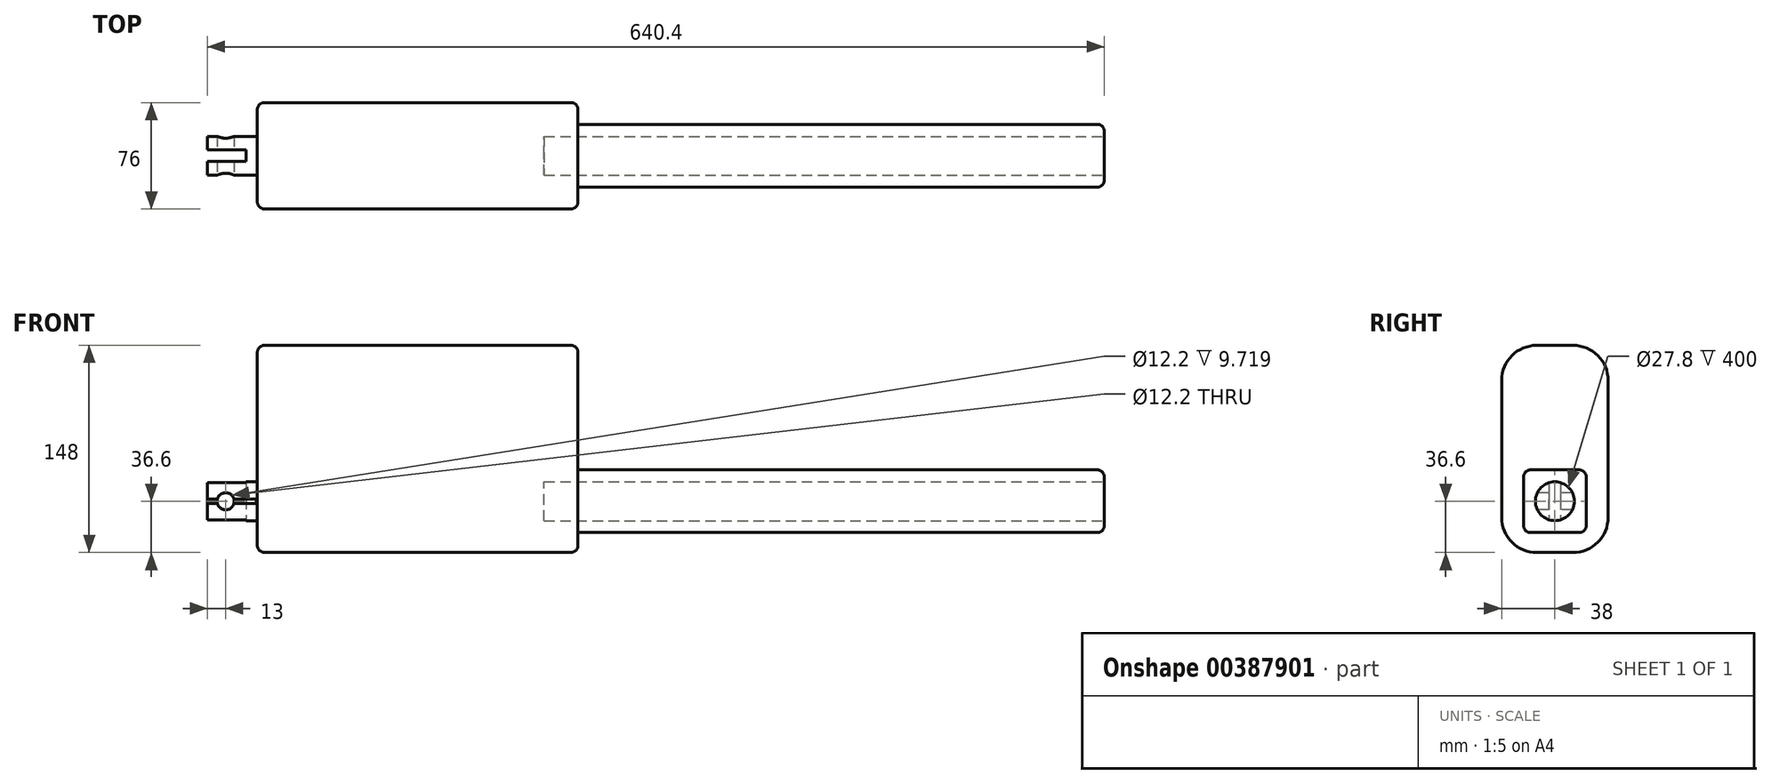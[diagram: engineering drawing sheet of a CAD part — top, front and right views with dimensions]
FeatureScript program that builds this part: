
annotation { "Feature Type Name" : "Feature", "Feature Type Description" : "" }
export const myFeature = defineFeature(function(context is Context, id is Id, definition is map)
    precondition{}
    {
        {
            var Q0;
            Q0=qCreatedBy(makeId("Front.planeOp"),FACE);
            var sketch = newSketch(context, id + "F0", { "sketchPlane" : qUnion([Q0])});
            skLineSegment(sketch, "E0.bottom", {"start": v(-114.5, 74) * mm, "end": v(114.5, 74) * mm});
            skLineSegment(sketch, "E0.top", {"start": v(-114.5, -74) * mm, "end": v(114.5, -74) * mm});
            skLineSegment(sketch, "E0.left", {"start": v(-114.5, 74) * mm, "end": v(-114.5, -74) * mm});
            skLineSegment(sketch, "E0.right", {"start": v(114.5, 74) * mm, "end": v(114.5, -74) * mm});
            skPoint(sketch, "E0.middle", {"position": v(0, 0) * mm});
            skSolve(sketch);
        }
        {
            var Q0;
            Q0=makeQuery(id+"F0.imprint","IMPRINT",FACE,{"disambiguationData":[TD([[makeQuery(id+"F0.imprint","IMPRINT",EDGE,{"derivedFrom":sQuery(id+"F0.wireOp",EDGE,"E0.bottom")}),-1.0]])]});
            extrude(context, id + "F1", {"entities" : qUnion([Q0]), "depth" : 76 * mm, "symmetric" : true});
        }
        {
            var Q0;
            Q0=makeQuery(id+"F1.opExtrude","SWEPT_FACE",FACE,{"disambiguationData":[OSD([sQuery(id+"F0.wireOp",EDGE,"E0.left")])]});
            var sketch = newSketch(context, id + "F2", { "sketchPlane" : qUnion([Q0])});
            skLineSegment(sketch, "E1", {"start": v(0, -74) * mm, "end": v(0, -37.4) * mm});
            skPoint(sketch, "E1.endSnap0", {"position": v(0, -74) * mm});
            skCircle(sketch, "E2", {"center": v(0, -37.4) * mm, "radius": 13.9 * mm});
            skSolve(sketch);
        }
        {
            var Q0;
            Q0=makeQuery(id+"F2.imprint","IMPRINT",FACE,{"disambiguationData":[TD([[makeQuery(id+"F2.imprint","IMPRINT",EDGE,{"derivedFrom":sQuery(id+"F2.wireOp",EDGE,"E2")}),1.0]])]});
            extrude(context, id + "F3", {"entities" : qUnion([Q0]), "operationType" : NewBodyOperationType.ADD, "depth" : 35.6 * mm});
        }
        {
            var Q0;
            Q0=makeQuery(id+"F3.opExtrude","CAP_FACE",FACE,{"disambiguationData":[OSD([sQuery(id+"F2.wireOp",EDGE,"E2")])],"isStart":false});
            var sketch = newSketch(context, id + "F4", { "sketchPlane" : qUnion([Q0])});
            skLineSegment(sketch, "E3.left", {"start": v(-13.82, -35.9) * mm, "end": v(-13.82, -38.9) * mm});
            skLineSegment(sketch, "E3.right", {"start": v(13.82, -35.9) * mm, "end": v(13.82, -38.9) * mm});
            skPoint(sketch, "E3.middle", {"position": v(0, -37.4) * mm});
            skSolve(sketch);
        }
        {
            var Q0;
            {var subQ0=sQuery(id+"F4.wireOp",EDGE,"E3.right");Q0=makeQuery(id+"F4.imprint","IMPRINT",FACE,{"disambiguationData":[TD([[makeQuery(id+"F4.imprint","IMPRINT",EDGE,{"derivedFrom":subQ0}),1.0]])]});}
            extrude(context, id + "F5", {"entities" : qUnion([Q0]), "operationType" : NewBodyOperationType.REMOVE, "oppositeDirection" : true, "depth" : 35 * mm});
        }
        {
            var Q0;
            Q0=makeQuery(id+"F5.boolean.opBoolean","COPY",FACE,{"derivedFrom":makeQuery(id+"F5.opExtrude","SWEPT_FACE",FACE,{"disambiguationData":[OSD([sQuery(id+"F4.wireOp",EDGE,"E3.right")])]})});
            var sketch = newSketch(context, id + "F6", { "sketchPlane" : qUnion([Q0])});
            skLineSegment(sketch, "E4", {"start": v(-150.1, -37.4) * mm, "end": v(-137.1, -37.4) * mm});
            skSolve(sketch);
        }
        {
            var Q0;
            Q0=sQuery(id+"F6.wireOp",VERTEX,"E4.end");
            var Q1;
            Q1=makeQuery(id+"F1.opExtrude","SWEPT_BODY",BODY,{"disambiguationData":[OSD([sQuery(id+"F0.wireOp",EDGE,"E0.bottom"),sQuery(id+"F0.wireOp",EDGE,"E0.top"),sQuery(id+"F0.wireOp",EDGE,"E0.left"),sQuery(id+"F0.wireOp",EDGE,"E0.right")])]});
            hole(context, id + "F7", {"style" : HoleStyle.SIMPLE, "endStyle" : HoleEndStyle.THROUGH, "holeDiameter" : 12.2 * mm, "isTappedThrough" : true, "tappedDepth" : 12 * mm, "tapClearance" : 3, "locations" : qUnion([Q0]), "scope" : qUnion([Q1])});
        }
        {
            var Q0;
            Q0=makeQuery(id+"F1.opExtrude","SWEPT_FACE",FACE,{"disambiguationData":[OSD([sQuery(id+"F0.wireOp",EDGE,"E0.right")])]});
            var sketch = newSketch(context, id + "F8", { "sketchPlane" : qUnion([Q0])});
            skLineSegment(sketch, "E5", {"start": v(0, -74) * mm, "end": v(0, -37.4) * mm});
            skLineSegment(sketch, "E6.bottom", {"start": v(-22.4, -15) * mm, "end": v(22.4, -15) * mm});
            skLineSegment(sketch, "E6.top", {"start": v(-22.4, -59.8) * mm, "end": v(22.4, -59.8) * mm});
            skLineSegment(sketch, "E6.left", {"start": v(-22.4, -15) * mm, "end": v(-22.4, -59.8) * mm});
            skLineSegment(sketch, "E6.right", {"start": v(22.4, -15) * mm, "end": v(22.4, -59.8) * mm});
            skPoint(sketch, "E6.middle", {"position": v(0, -37.4) * mm});
            skSolve(sketch);
        }
        {
            var Q0;
            Q0=makeQuery(id+"F8.imprint","IMPRINT",FACE,{"disambiguationData":[TD([[makeQuery(id+"F8.imprint","IMPRINT",EDGE,{"derivedFrom":sQuery(id+"F8.wireOp",EDGE,"E6.bottom")}),-1.0]])]});
            extrude(context, id + "F9", {"entities" : qUnion([Q0]), "operationType" : NewBodyOperationType.ADD, "depth" : 375.8 * mm});
        }
        {
            var Q0;
            Q0=makeQuery(id+"F9.opExtrude","CAP_FACE",FACE,{"disambiguationData":[OSD([sQuery(id+"F8.wireOp",EDGE,"E6.bottom"),sQuery(id+"F8.wireOp",EDGE,"E6.top"),sQuery(id+"F8.wireOp",EDGE,"E6.left"),sQuery(id+"F8.wireOp",EDGE,"E6.right")])],"isStart":false});
            var sketch = newSketch(context, id + "F10", { "sketchPlane" : qUnion([Q0])});
            skLineSegment(sketch, "E7", {"start": v(0, -15) * mm, "end": v(0, -37.4) * mm});
            skPoint(sketch, "E7.endSnap0", {"position": v(0, -15) * mm});
            skCircle(sketch, "E8", {"center": v(0, -37.4) * mm, "radius": 13.9 * mm});
            skSolve(sketch);
        }
        {
            var Q0;
            Q0=makeQuery(id+"F1.opExtrude","CAP_EDGE",EDGE,{"disambiguationData":[OSD([sQuery(id+"F0.wireOp",EDGE,"E0.bottom")])],"isStart":false});
            var Q1;
            Q1=makeQuery(id+"F1.opExtrude","CAP_EDGE",EDGE,{"disambiguationData":[OSD([sQuery(id+"F0.wireOp",EDGE,"E0.bottom")])],"isStart":true});
            var Q2;
            Q2=makeQuery(id+"F1.opExtrude","CAP_EDGE",EDGE,{"disambiguationData":[OSD([sQuery(id+"F0.wireOp",EDGE,"E0.top")])],"isStart":false});
            var Q3;
            Q3=makeQuery(id+"F1.opExtrude","CAP_EDGE",EDGE,{"disambiguationData":[OSD([sQuery(id+"F0.wireOp",EDGE,"E0.top")])],"isStart":true});
            fillet(context, id + "F11", {"entities" : qUnion([Q0, Q1, Q2, Q3]), "radius" : 25 * mm, "tangentPropagation" : true, "allowEdgeOverflow" : false});
        }
        {
            var Q0;
            Q0=makeQuery(id+"F9.opExtrude","SWEPT_EDGE",EDGE,{"disambiguationData":[OSD([sQuery(id+"F8.wireOp",EDGE,"E6.bottom"),sQuery(id+"F8.wireOp",EDGE,"E6.left")])]});
            var Q1;
            Q1=makeQuery(id+"F9.opExtrude","SWEPT_EDGE",EDGE,{"disambiguationData":[OSD([sQuery(id+"F8.wireOp",EDGE,"E6.bottom"),sQuery(id+"F8.wireOp",EDGE,"E6.right")])]});
            var Q2;
            Q2=makeQuery(id+"F9.opExtrude","SWEPT_EDGE",EDGE,{"disambiguationData":[OSD([sQuery(id+"F8.wireOp",EDGE,"E6.top"),sQuery(id+"F8.wireOp",EDGE,"E6.left")])]});
            var Q3;
            Q3=makeQuery(id+"F9.opExtrude","SWEPT_EDGE",EDGE,{"disambiguationData":[OSD([sQuery(id+"F8.wireOp",EDGE,"E6.top"),sQuery(id+"F8.wireOp",EDGE,"E6.right")])]});
            var Q4;
            Q4=makeQuery(id+"F1.opExtrude","CAP_EDGE",EDGE,{"disambiguationData":[OSD([sQuery(id+"F0.wireOp",EDGE,"E0.right")])],"isStart":true});
            var Q5;
            Q5=makeQuery(id+"F1.opExtrude","CAP_EDGE",EDGE,{"disambiguationData":[OSD([sQuery(id+"F0.wireOp",EDGE,"E0.left")])],"isStart":true});
            var Q6;
            Q6=makeQuery(id+"F9.opExtrude","CAP_EDGE",EDGE,{"disambiguationData":[OSD([sQuery(id+"F8.wireOp",EDGE,"E6.right")])],"isStart":false});
            var Q7;
            Q7=makeQuery(id+"F9.opExtrude","CAP_FACE",FACE,{"disambiguationData":[OSD([sQuery(id+"F8.wireOp",EDGE,"E6.bottom"),sQuery(id+"F8.wireOp",EDGE,"E6.top"),sQuery(id+"F8.wireOp",EDGE,"E6.left"),sQuery(id+"F8.wireOp",EDGE,"E6.right")])],"isStart":false});
            fillet(context, id + "F12", {"entities" : qUnion([Q0, Q1, Q2, Q3, Q4, Q5, Q6, Q7]), "radius" : 5 * mm, "tangentPropagation" : true, "allowEdgeOverflow" : false});
        }
        {
            var Q0;
            Q0=makeQuery(id+"F10.imprint","IMPRINT",FACE,{"disambiguationData":[TD([[makeQuery(id+"F10.imprint","IMPRINT",EDGE,{"derivedFrom":sQuery(id+"F10.wireOp",EDGE,"E8")}),1.0]])]});
            extrude(context, id + "F13", {"entities" : qUnion([Q0]), "operationType" : NewBodyOperationType.REMOVE, "oppositeDirection" : true, "depth" : 400 * mm});
        }
        {
            var Q0;
            Q0=makeQuery(id+"F3.opExtrude","CAP_FACE",FACE,{"disambiguationData":[OSD([sQuery(id+"F2.wireOp",EDGE,"E2")])],"isStart":false});
            var sketch = newSketch(context, id + "F14", { "sketchPlane" : qUnion([Q0])});
            skLineSegment(sketch, "E9.bottom", {"start": v(-4.1, 11.75) * mm, "end": v(4.1, 11.75) * mm});
            skLineSegment(sketch, "E9.top", {"start": v(-4.1, -86.55) * mm, "end": v(4.1, -86.55) * mm});
            skLineSegment(sketch, "E9.left", {"start": v(-4.1, 11.75) * mm, "end": v(-4.1, -86.55) * mm});
            skLineSegment(sketch, "E9.right", {"start": v(4.1, 11.75) * mm, "end": v(4.1, -86.55) * mm});
            skPoint(sketch, "E9.middle", {"position": v(0, -37.4) * mm});
            skSolve(sketch);
        }
        {
            var Q0;
            {var subQ0=sQuery(id+"F14.wireOp",EDGE,"E9.left");var subQ1=makeQuery(id+"F3.opExtrude","CAP_EDGE",EDGE,{"disambiguationData":[OSD([sQuery(id+"F2.wireOp",EDGE,"E2")])],"isStart":false});var subQ2=makeQuery(id+"F14.imprint","INTERSECT",VERTEX,{"disambiguationData":[OD(0.0)],"derivedFrom":[subQ1,subQ0]});Q0=makeQuery(id+"F14.imprint","IMPRINT",FACE,{"disambiguationData":[TD([[makeQuery(id+"F14.imprint","IMPRINT",EDGE,{"disambiguationData":[TD([[subQ2,-1.0]])],"derivedFrom":subQ0}),1.0]])]});}
            extrude(context, id + "F15", {"entities" : qUnion([Q0]), "operationType" : NewBodyOperationType.REMOVE, "oppositeDirection" : true, "depth" : 27.5 * mm});
        }
    });
